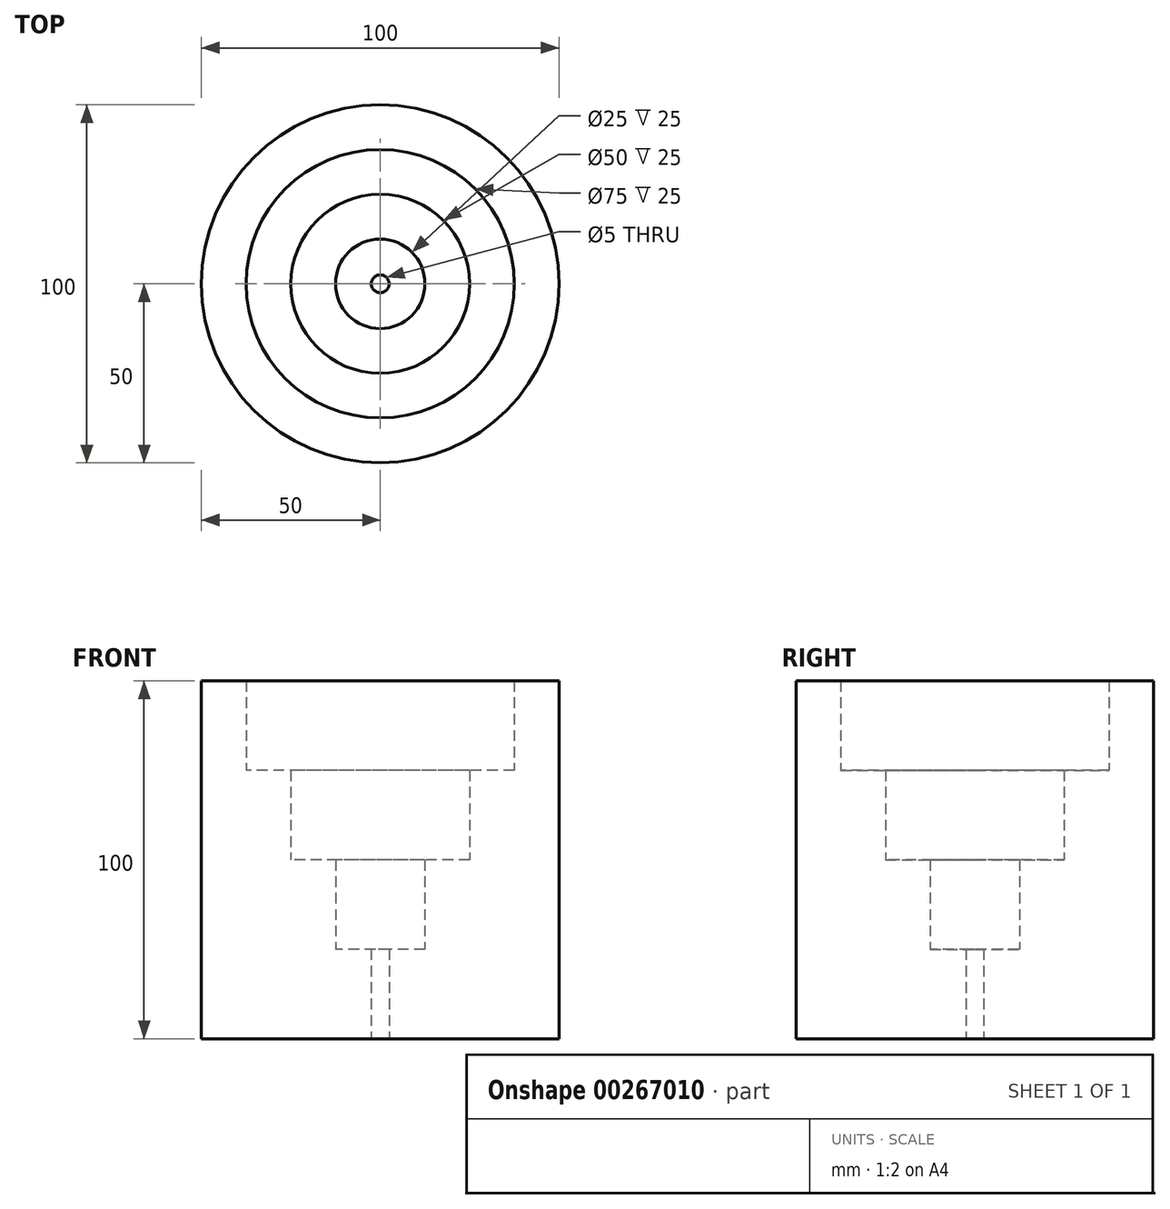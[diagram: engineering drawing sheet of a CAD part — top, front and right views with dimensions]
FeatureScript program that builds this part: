
annotation { "Feature Type Name" : "Feature", "Feature Type Description" : "" }
export const myFeature = defineFeature(function(context is Context, id is Id, definition is map)
    precondition{}
    {
        {
            var Q0;
            Q0=qCreatedBy(makeId("Top.planeOp"),FACE);
            var sketch = newSketch(context, id + "F0", { "sketchPlane" : qUnion([Q0])});
            skCircle(sketch, "E0", {"center": v(0, 0) * mm, "radius": 50 * mm});
            skCircle(sketch, "E1", {"center": v(0, 0) * mm, "radius": 37.5 * mm});
            skCircle(sketch, "E2", {"center": v(0, 0) * mm, "radius": 25 * mm});
            skCircle(sketch, "E3", {"center": v(0, 0) * mm, "radius": 12.5 * mm});
            skSolve(sketch);
        }
        {
            var Q0;
            Q0=makeQuery(id+"F0.imprint","IMPRINT",FACE,{"disambiguationData":[TD([[makeQuery(id+"F0.imprint","IMPRINT",EDGE,{"derivedFrom":sQuery(id+"F0.wireOp",EDGE,"E3")}),1.0]])]});
            extrude(context, id + "F1", {"entities" : qUnion([Q0]), "depth" : 25 * mm});
        }
        {
            var Q0;
            Q0=makeQuery(id+"F0.imprint","IMPRINT",FACE,{"disambiguationData":[TD([[makeQuery(id+"F0.imprint","IMPRINT",EDGE,{"derivedFrom":sQuery(id+"F0.wireOp",EDGE,"E2")}),1.0]])]});
            extrude(context, id + "F2", {"entities" : qUnion([Q0]), "operationType" : NewBodyOperationType.ADD, "depth" : 50 * mm});
        }
        {
            var Q0;
            Q0=makeQuery(id+"F0.imprint","IMPRINT",FACE,{"disambiguationData":[TD([[makeQuery(id+"F0.imprint","IMPRINT",EDGE,{"derivedFrom":sQuery(id+"F0.wireOp",EDGE,"E1")}),1.0]])]});
            extrude(context, id + "F3", {"entities" : qUnion([Q0]), "operationType" : NewBodyOperationType.ADD, "depth" : 75 * mm});
        }
        {
            var Q0;
            Q0=makeQuery(id+"F0.imprint","IMPRINT",FACE,{"disambiguationData":[TD([[makeQuery(id+"F0.imprint","IMPRINT",EDGE,{"derivedFrom":sQuery(id+"F0.wireOp",EDGE,"E0")}),1.0]])]});
            extrude(context, id + "F4", {"entities" : qUnion([Q0]), "operationType" : NewBodyOperationType.ADD, "depth" : 100 * mm});
        }
        {
            var Q0;
            Q0=sQuery(id+"F0.wireOp",VERTEX,"E0.center");
            var Q1;
            Q1=makeQuery(id+"F1.opExtrude","SWEPT_BODY",BODY,{"disambiguationData":[OSD([sQuery(id+"F0.wireOp",EDGE,"E3")])]});
            hole(context, id + "F5", {"style" : HoleStyle.SIMPLE, "endStyle" : HoleEndStyle.THROUGH, "oppositeDirection" : true, "holeDiameter" : 5 * mm, "tappedDepth" : 12 * mm, "tapClearance" : 3, "locations" : qUnion([Q0]), "scope" : qUnion([Q1])});
        }
    });
